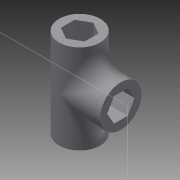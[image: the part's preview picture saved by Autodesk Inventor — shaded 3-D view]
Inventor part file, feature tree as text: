
AUTODESK INVENTOR PART (.ipt)
format: ipt  version: 2015 SP1 (Build 190203100, 203)  size: 260,608 bytes
history: native  units: mm
features: sketch x9, extrude x7, projected_geometry x3, other x1, plane x1, fillet x1
ambient origin geometry x8: Origin, YZ Plane, XZ Plane, XY Plane, X Axis, Y Axis, Z Axis, Center Point
bodies: Body1 (feature_tree)
feature tree (22):
  other  "Sólido1"
  extrude  "Extrusión1"  Depth=4.0mm
  sketch  "Boceto2"  dims[d2=7.0mm d3=0.0mm d4=12.0mm d5=0.0mm]
  extrude  "Extrusión2"  Depth=12.0mm TaperAngle=0.0deg
  plane  "Plano de trabajo1"
  extrude  "Extrusión3"  Depth=12.0mm
  extrude  "Extrusión6"  Depth=12.0mm TaperAngle=0.0deg
  sketch  "Boceto8"  dims[d20=7.0mm d21=0.0mm d22=6.0mm]
  extrude  "Extrusión7"  Depth=7.0mm TaperAngle=0.0deg
  extrude  "Extrusión8"  Depth=6.0mm
  extrude  "Extrusión9"  [1 undecoded]
  fillet  "Empalme1"  [1 undecoded]
  sketch  "Boceto1"  dims[d0=12.0mm d1=4.0mm]
  sketch  "Boceto3"  dims[d6=6.0mm d7=12.0mm]
  projected_geometry  "Contorno proyectado1"
  sketch  "Boceto4"  dims[d8=12.0mm d9=0.0mm d14=12.0mm d15=0.0mm]
  projected_geometry  "Contorno proyectado2"
  sketch  "Boceto7"  dims[d16=12.0mm d17=0.0mm d18=7.0mm d19=0.0mm]
  sketch  "Boceto9"
  projected_geometry  "Contorno proyectado5"
  sketch  "Boceto10"
  sketch  "Boceto11"
note: 2 required parameter values undecoded (feature->parameter linkage not recoverable at this tier; creation-order binding heuristic only, values carry confidence <= 0.55)
